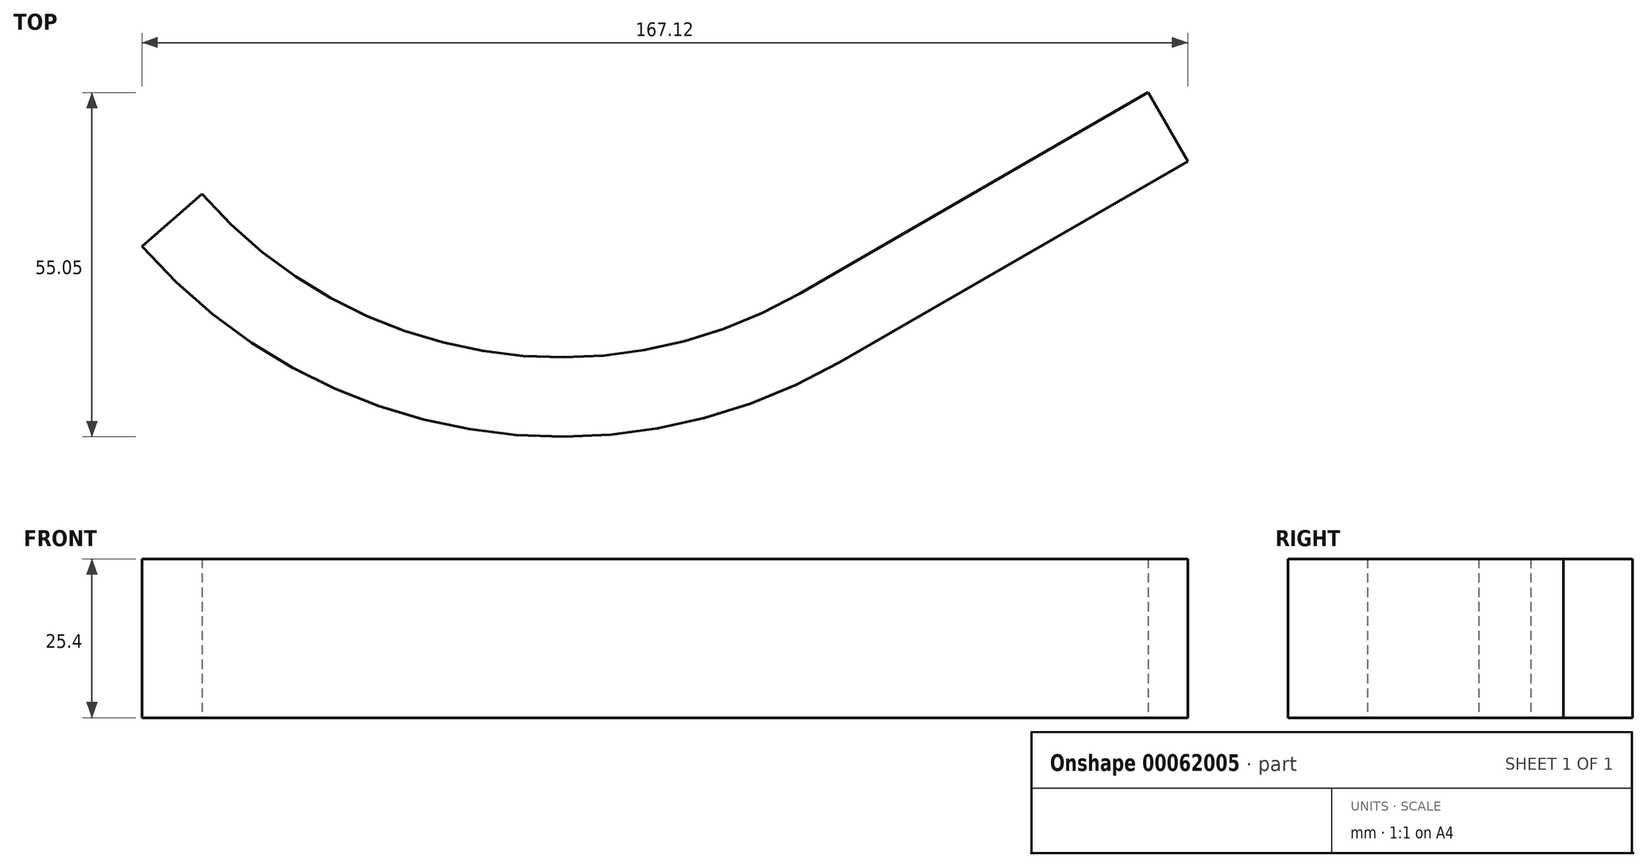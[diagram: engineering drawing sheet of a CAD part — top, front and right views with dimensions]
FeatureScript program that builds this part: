
annotation { "Feature Type Name" : "Feature", "Feature Type Description" : "" }
export const myFeature = defineFeature(function(context is Context, id is Id, definition is map)
    precondition{}
    {
        {
            var Q0;
            Q0=qCreatedBy(makeId("Top.planeOp"),FACE);
            var sketch = newSketch(context, id + "F0", { "sketchPlane" : qUnion([Q0])});
            skLineSegment(sketch, "E0.bottom", {"start": v(0, 0) * mm, "end": v(426.12, 0) * mm});
            skLineSegment(sketch, "E0.top", {"start": v(0, 496.7) * mm, "end": v(426.12, 496.7) * mm});
            skLineSegment(sketch, "E0.left", {"start": v(0, 0) * mm, "end": v(0, 496.7) * mm});
            skLineSegment(sketch, "E0.right", {"start": v(426.12, 0) * mm, "end": v(426.12, 183) * mm});
            skLineSegment(sketch, "E1", {"start": v(0, 496.7) * mm, "end": v(274.92, 181.43) * mm});
            skLineSegment(sketch, "E2", {"start": v(370.45, 165.52) * mm, "end": v(426.12, 197.66) * mm});
            skLineSegment(sketch, "E3", {"start": v(316.14, 134.16) * mm, "end": v(426.12, 134.16) * mm, "construction": true});
            skPoint(sketch, "E4.visualSharp", {"position": v(316.14, 134.16) * mm});
            skArc(sketch, "E4.filletArc", {"start": v(274.92, 181.43) * mm, "mid": v(319.83, 156.35) * mm, "end": v(370.45, 165.52) * mm});
            skLineSegment(sketch, "E5.0", {"start": v(376.8, 154.52) * mm, "end": v(432.47, 186.66) * mm});
            skArc(sketch, "E5.1", {"start": v(265.35, 173.08) * mm, "mid": v(317.75, 143.82) * mm, "end": v(376.8, 154.52) * mm});
            skLineSegment(sketch, "E5.2", {"start": v(-4.38, 482.4) * mm, "end": v(265.35, 173.08) * mm});
            skLineSegment(sketch, "E6", {"start": v(426.12, 197.66) * mm, "end": v(432.47, 186.66) * mm});
            skLineSegment(sketch, "E7", {"start": v(0, 496.7) * mm, "end": v(-4.38, 482.4) * mm});
            skLineSegment(sketch, "E8", {"start": v(274.92, 181.43) * mm, "end": v(265.35, 173.08) * mm});
            skLineSegment(sketch, "E9.trimOffspring", {"start": v(426.12, 197.66) * mm, "end": v(426.12, 496.7) * mm});
            skSolve(sketch);
        }
        {
            var Q0;
            Q0=makeQuery(id+"F0.imprint","IMPRINT",FACE,{"disambiguationData":[TD([[makeQuery(id+"F0.imprint","IMPRINT",EDGE,{"derivedFrom":sQuery(id+"F0.wireOp",EDGE,"E2")}),-1.0]])]});
            extrude(context, id + "F1", {"entities" : qUnion([Q0]), "depth" : 25.4 * mm});
        }
    });
